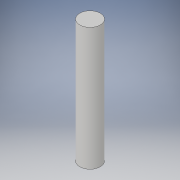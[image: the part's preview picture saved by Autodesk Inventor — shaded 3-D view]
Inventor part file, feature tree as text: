
AUTODESK INVENTOR PART (.ipt)
format: ipt  version: 2019 (Build 230136000, 136)  size: 90,112 bytes
history: native  units: mm
features: extrude x1, sketch x1
ambient origin geometry x8: Origin, YZ Plane, XZ Plane, XY Plane, X Axis, Y Axis, Z Axis, Center Point
bodies: Solid1 (feature_tree)
feature tree (2):
  extrude  "Extrusion1"  Depth=60.0mm TaperAngle=0.0deg
  sketch  "Sketch1"  dims[d0=10.0mm d1=60.0mm d2=0.0mm]
